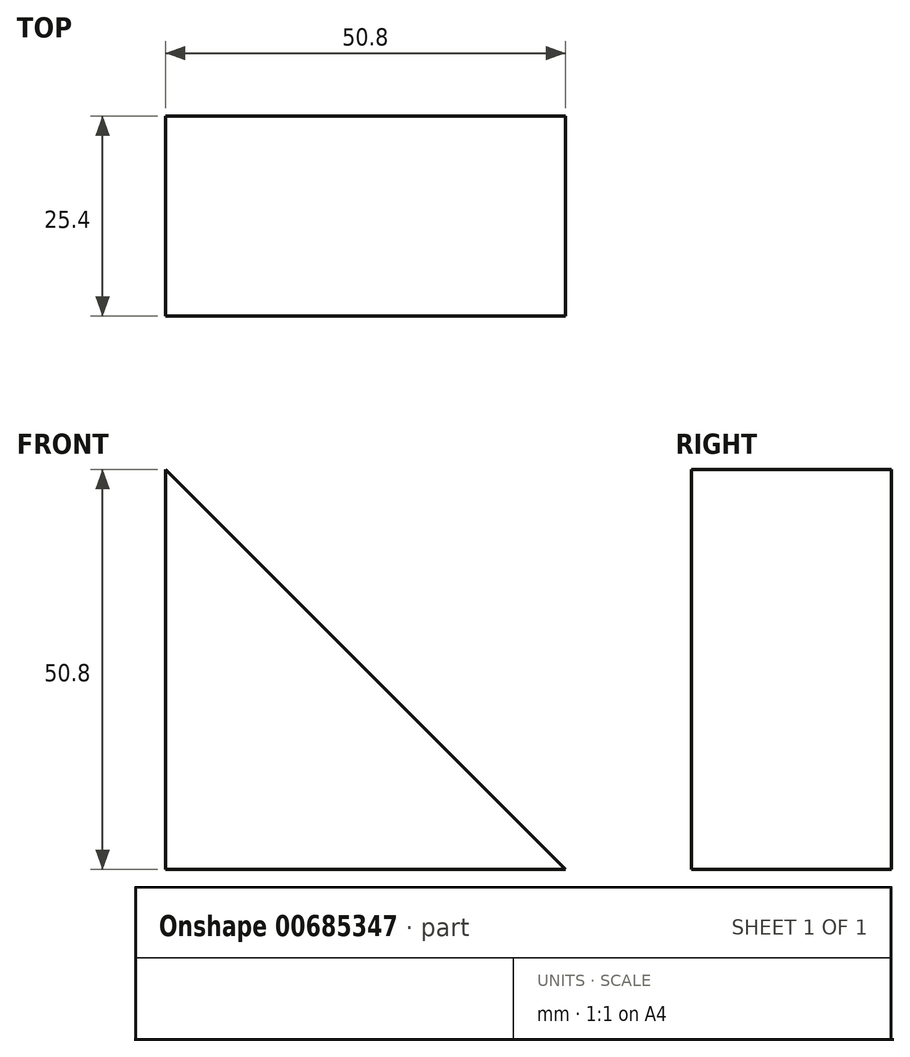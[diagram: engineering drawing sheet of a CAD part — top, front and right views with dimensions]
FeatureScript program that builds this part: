
annotation { "Feature Type Name" : "Feature", "Feature Type Description" : "" }
export const myFeature = defineFeature(function(context is Context, id is Id, definition is map)
    precondition{}
    {
        {
            var Q0;
            Q0=qCreatedBy(makeId("Front.planeOp"),FACE);
            var sketch = newSketch(context, id + "F0", { "sketchPlane" : qUnion([Q0])});
            skLineSegment(sketch, "E0", {"start": v(-50.8, 0) * mm, "end": v(-50.8, 50.8) * mm});
            skLineSegment(sketch, "E1", {"start": v(-50.8, 0) * mm, "end": v(0, 0) * mm});
            skLineSegment(sketch, "E2", {"start": v(-50.8, 50.8) * mm, "end": v(0, 0) * mm});
            skSolve(sketch);
        }
        {
            var Q0;
            Q0=makeQuery(id+"F0.imprint","IMPRINT",FACE,{"disambiguationData":[TD([[makeQuery(id+"F0.imprint","IMPRINT",EDGE,{"derivedFrom":sQuery(id+"F0.wireOp",EDGE,"E0")}),-1.0]])]});
            extrude(context, id + "F1", {"entities" : qUnion([Q0]), "depth" : 25.4 * mm, "offsetDistance" : 25.4 * mm});
        }
    });
